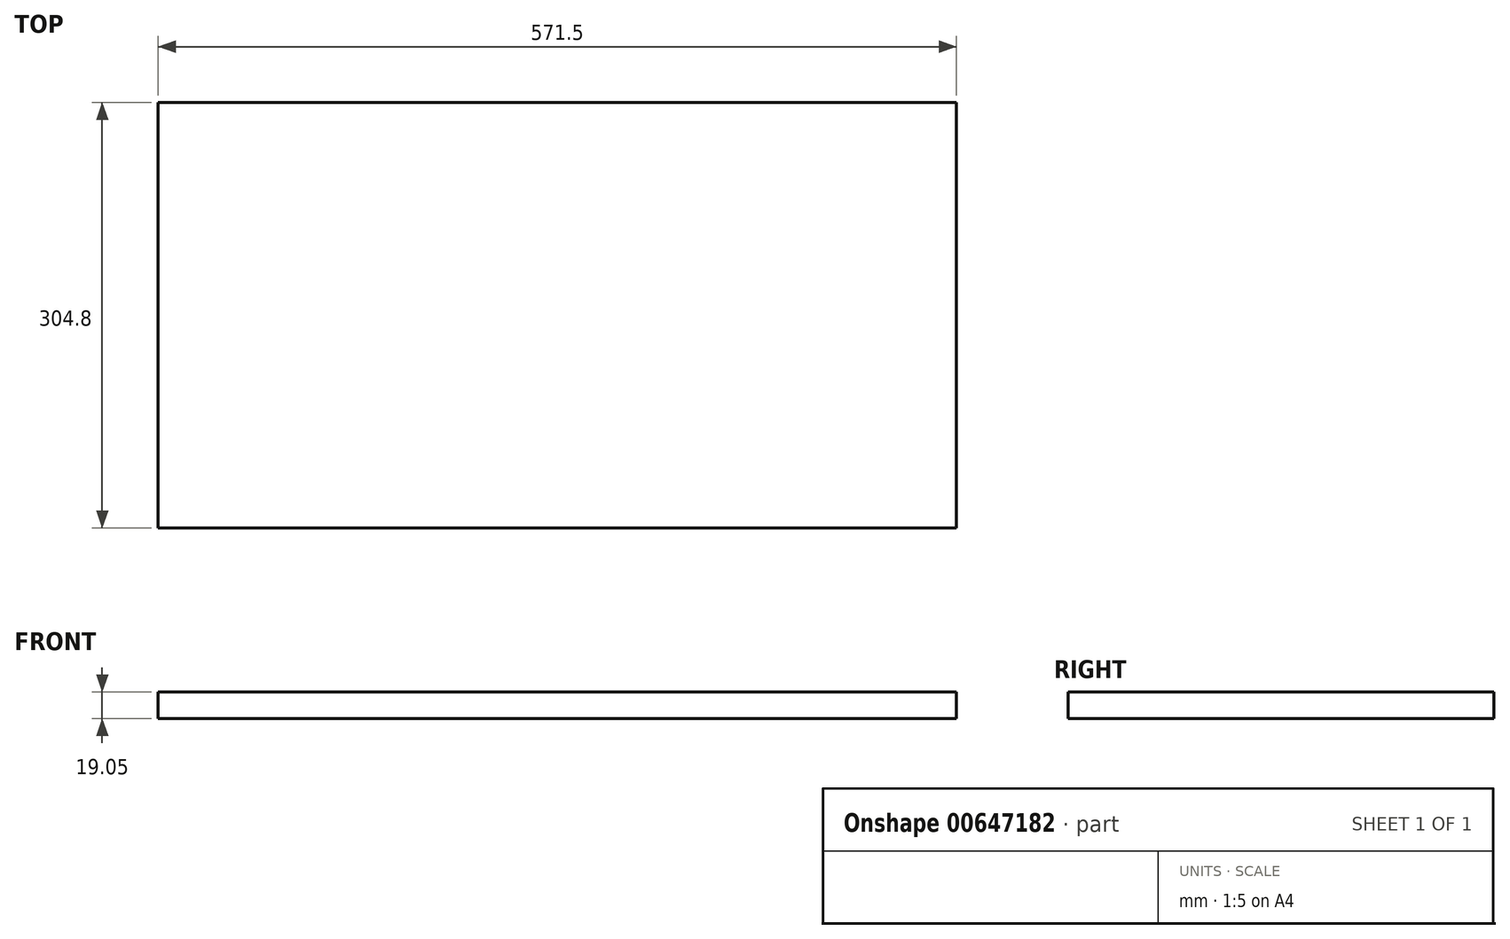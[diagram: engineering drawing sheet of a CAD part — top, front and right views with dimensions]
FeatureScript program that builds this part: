
annotation { "Feature Type Name" : "Feature", "Feature Type Description" : "" }
export const myFeature = defineFeature(function(context is Context, id is Id, definition is map)
    precondition{}
    {
        {
            var Q0;
            Q0=qCreatedBy(makeId("Top.planeOp"),FACE);
            var sketch = newSketch(context, id + "F0", { "sketchPlane" : qUnion([Q0])});
            skLineSegment(sketch, "E0.bottom", {"start": v(-285.75, 152.4) * mm, "end": v(285.75, 152.4) * mm});
            skLineSegment(sketch, "E0.top", {"start": v(-285.75, -152.4) * mm, "end": v(285.75, -152.4) * mm});
            skLineSegment(sketch, "E0.left", {"start": v(-285.75, 152.4) * mm, "end": v(-285.75, -152.4) * mm});
            skLineSegment(sketch, "E0.right", {"start": v(285.75, 152.4) * mm, "end": v(285.75, -152.4) * mm});
            skPoint(sketch, "E0.middle", {"position": v(0, 0) * mm});
            skPoint(sketch, "E1.endSnap0", {"position": v(0, -152.4) * mm});
            skSolve(sketch);
        }
        {
            var Q0;
            Q0=makeQuery(id+"F0.imprint","IMPRINT",FACE,{"disambiguationData":[TD([[makeQuery(id+"F0.imprint","IMPRINT",EDGE,{"derivedFrom":sQuery(id+"F0.wireOp",EDGE,"E0.bottom")}),-1.0]])]});
            var Q1;
            {var subQ3=sQuery(id+"F0.wireOp",EDGE,"E1");Q1=makeQuery(id+"F0.imprint","IMPRINT",FACE,{"disambiguationData":[TD([[makeQuery(id+"F0.imprint","IMPRINT",EDGE,{"derivedFrom":subQ3}),-1.0]])]});}
            var Q2;
            {var subQ3=sQuery(id+"F0.wireOp",EDGE,"E1");Q2=makeQuery(id+"F0.imprint","IMPRINT",FACE,{"disambiguationData":[TD([[makeQuery(id+"F0.imprint","IMPRINT",EDGE,{"derivedFrom":subQ3}),1.0]])]});}
            extrude(context, id + "F1", {"entities" : qUnion([Q0, Q1, Q2]), "depth" : 19.05 * mm, "offsetDistance" : 25.4 * mm});
        }
    });
